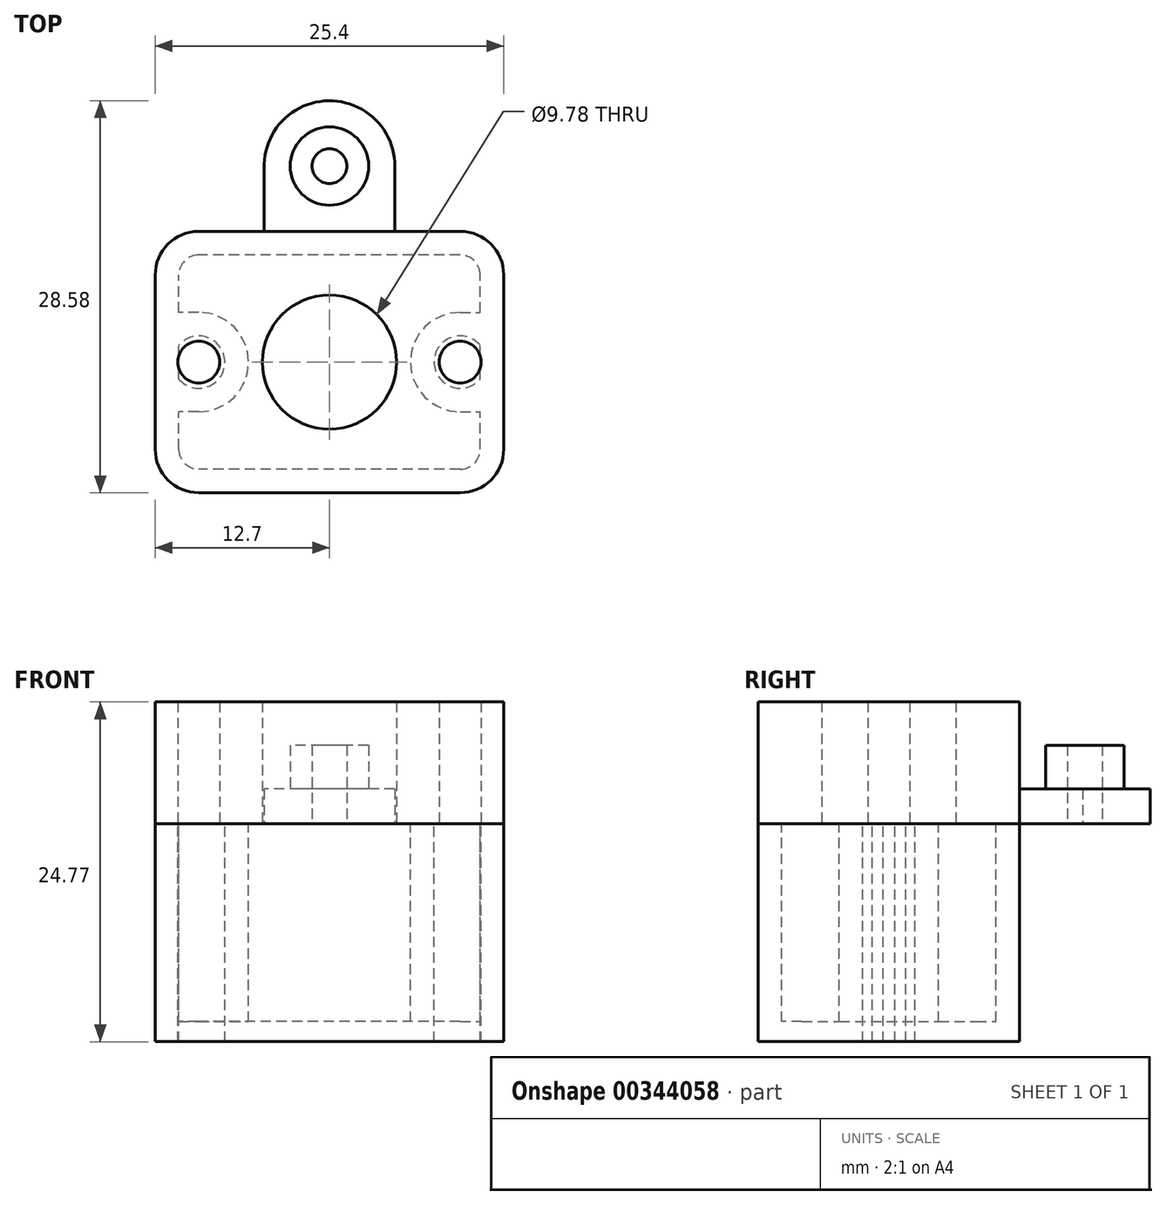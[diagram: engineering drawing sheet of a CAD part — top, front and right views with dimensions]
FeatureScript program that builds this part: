
annotation { "Feature Type Name" : "Feature", "Feature Type Description" : "" }
export const myFeature = defineFeature(function(context is Context, id is Id, definition is map)
    precondition{}
    {
        {
            var Q0;
            Q0=qCreatedBy(makeId("Top.planeOp"),FACE);
            var sketch = newSketch(context, id + "F0", { "sketchPlane" : qUnion([Q0])});
            skCircle(sketch, "E0", {"center": v(0, 0) * mm, "radius": 4.89 * mm});
            skLineSegment(sketch, "E1.bottom", {"start": v(9.52, -9.52) * mm, "end": v(-9.53, -9.53) * mm});
            skLineSegment(sketch, "E1.top", {"start": v(9.53, 9.53) * mm, "end": v(-9.53, 9.52) * mm});
            skLineSegment(sketch, "E1.left", {"start": v(12.7, -6.35) * mm, "end": v(12.7, 6.35) * mm});
            skLineSegment(sketch, "E1.right", {"start": v(-12.7, -6.35) * mm, "end": v(-12.7, 6.35) * mm});
            skPoint(sketch, "E2.visualSharp", {"position": v(-12.7, -9.53) * mm});
            skArc(sketch, "E2.filletArc", {"start": v(-12.7, -6.35) * mm, "mid": v(-11.77, -8.6) * mm, "end": v(-9.53, -9.53) * mm});
            skPoint(sketch, "E3.visualSharp", {"position": v(-12.7, 9.52) * mm});
            skArc(sketch, "E3.filletArc", {"start": v(-9.53, 9.52) * mm, "mid": v(-11.77, 8.6) * mm, "end": v(-12.7, 6.35) * mm});
            skPoint(sketch, "E4.visualSharp", {"position": v(12.7, -9.52) * mm});
            skArc(sketch, "E4.filletArc", {"start": v(9.52, -9.52) * mm, "mid": v(11.77, -8.6) * mm, "end": v(12.7, -6.35) * mm});
            skPoint(sketch, "E5.visualSharp", {"position": v(12.7, 9.53) * mm});
            skArc(sketch, "E5.filletArc", {"start": v(12.7, 6.35) * mm, "mid": v(11.77, 8.6) * mm, "end": v(9.53, 9.53) * mm});
            skCircle(sketch, "E6", {"center": v(-9.53, 0) * mm, "radius": 1.52 * mm});
            skPoint(sketch, "E6.centerSnap0", {"position": v(-12.7, 0) * mm});
            skCircle(sketch, "E7.MirrorC", {"center": v(9.53, 0) * mm, "radius": 1.52 * mm});
            skCircle(sketch, "E8", {"center": v(0, 14.29) * mm, "radius": 4.76 * mm});
            skLineSegment(sketch, "E9", {"start": v(-4.76, 14.12) * mm, "end": v(-4.76, 9.53) * mm});
            skLineSegment(sketch, "E10.bottom", {"start": v(4.76, 9.53) * mm, "end": v(-4.76, 9.53) * mm});
            skLineSegment(sketch, "E11", {"start": v(4.76, 9.53) * mm, "end": v(4.76, 14.26) * mm});
            skCircle(sketch, "E12", {"center": v(0, 14.29) * mm, "radius": 2.86 * mm});
            skCircle(sketch, "E13", {"center": v(0, 14.29) * mm, "radius": 1.27 * mm});
            skSolve(sketch);
        }
        {
            var Q0;
            Q0=makeQuery(id+"F0.imprint","IMPRINT",FACE,{"disambiguationData":[TD([[makeQuery(id+"F0.imprint","IMPRINT",EDGE,{"derivedFrom":sQuery(id+"F0.wireOp",EDGE,"E0")}),-1.0]])]});
            extrude(context, id + "F1", {"entities" : qUnion([Q0]), "depth" : 8.9 * mm});
        }
        {
            var Q0;
            {var subQ0=sQuery(id+"F0.wireOp",EDGE,"E11");Q0=makeQuery(id+"F0.imprint","IMPRINT",FACE,{"disambiguationData":[TD([[makeQuery(id+"F0.imprint","IMPRINT",EDGE,{"derivedFrom":subQ0}),1.0]])]});}
            var Q1;
            {var subQ0=sQuery(id+"F0.wireOp",EDGE,"E9");Q1=makeQuery(id+"F0.imprint","IMPRINT",FACE,{"disambiguationData":[TD([[makeQuery(id+"F0.imprint","IMPRINT",EDGE,{"derivedFrom":subQ0}),1.0]])]});}
            var Q2;
            Q2=makeQuery(id+"F0.imprint","IMPRINT",FACE,{"disambiguationData":[TD([[makeQuery(id+"F0.imprint","IMPRINT",EDGE,{"derivedFrom":sQuery(id+"F0.wireOp",EDGE,"E12")}),-1.0]])]});
            extrude(context, id + "F2", {"entities" : qUnion([Q0, Q1, Q2]), "operationType" : NewBodyOperationType.ADD, "depth" : 2.54 * mm});
        }
        {
            var Q0;
            Q0=makeQuery(id+"F0.imprint","IMPRINT",FACE,{"disambiguationData":[TD([[makeQuery(id+"F0.imprint","IMPRINT",EDGE,{"derivedFrom":sQuery(id+"F0.wireOp",EDGE,"E12")}),1.0]])]});
            extrude(context, id + "F3", {"entities" : qUnion([Q0]), "operationType" : NewBodyOperationType.ADD, "depth" : 5.7 * mm});
        }
        {
            var Q0;
            Q0=makeQuery(id+"F0.imprint","IMPRINT",FACE,{"disambiguationData":[TD([[makeQuery(id+"F0.imprint","IMPRINT",EDGE,{"derivedFrom":sQuery(id+"F0.wireOp",EDGE,"E0")}),-1.0]])]});
            var sketch = newSketch(context, id + "F4", { "sketchPlane" : qUnion([Q0])});
            skLineSegment(sketch, "E14.0", {"start": v(9.52, -9.52) * mm, "end": v(-9.53, -9.53) * mm});
            skArc(sketch, "E15.0", {"start": v(9.52, -9.52) * mm, "mid": v(11.77, -8.6) * mm, "end": v(12.7, -6.35) * mm});
            skLineSegment(sketch, "E16.0", {"start": v(12.7, -6.35) * mm, "end": v(12.7, 6.35) * mm});
            skArc(sketch, "E17.0", {"start": v(12.7, 6.35) * mm, "mid": v(11.77, 8.6) * mm, "end": v(9.53, 9.53) * mm});
            skLineSegment(sketch, "E18.0", {"start": v(9.53, 9.53) * mm, "end": v(-9.53, 9.52) * mm});
            skArc(sketch, "E19.0", {"start": v(-9.53, 9.52) * mm, "mid": v(-11.77, 8.6) * mm, "end": v(-12.7, 6.35) * mm});
            skLineSegment(sketch, "E20.0", {"start": v(-12.7, -6.35) * mm, "end": v(-12.7, 6.35) * mm});
            skArc(sketch, "E21.0", {"start": v(-12.7, -6.35) * mm, "mid": v(-11.77, -8.6) * mm, "end": v(-9.53, -9.53) * mm});
            skArc(sketch, "E22", {"start": v(10.99, 1.22) * mm, "mid": v(7.62, 0) * mm, "end": v(10.99, -1.22) * mm});
            skArc(sketch, "E23", {"start": v(-10.99, -1.22) * mm, "mid": v(-7.62, 0) * mm, "end": v(-10.99, 1.22) * mm});
            skArc(sketch, "E24.0", {"start": v(-10.99, -6.35) * mm, "mid": v(-10.56, -7.38) * mm, "end": v(-9.53, -7.81) * mm});
            skLineSegment(sketch, "E24.1", {"start": v(9.52, -7.81) * mm, "end": v(-9.53, -7.81) * mm});
            skLineSegment(sketch, "E24.2", {"start": v(-10.99, -6.35) * mm, "end": v(-10.99, 6.35) * mm});
            skArc(sketch, "E24.3", {"start": v(9.52, -7.81) * mm, "mid": v(10.56, -7.38) * mm, "end": v(10.99, -6.35) * mm});
            skArc(sketch, "E24.4", {"start": v(-9.53, 7.81) * mm, "mid": v(-10.56, 7.38) * mm, "end": v(-10.99, 6.35) * mm});
            skLineSegment(sketch, "E24.5", {"start": v(9.53, 7.81) * mm, "end": v(-9.53, 7.81) * mm});
            skArc(sketch, "E24.6", {"start": v(10.99, 6.35) * mm, "mid": v(10.56, 7.38) * mm, "end": v(9.53, 7.81) * mm});
            skLineSegment(sketch, "E24.7", {"start": v(10.99, -6.35) * mm, "end": v(10.99, 6.35) * mm});
            skArc(sketch, "E25.0", {"start": v(-9.53, -3.62) * mm, "mid": v(-5.9, 0) * mm, "end": v(-9.53, 3.62) * mm});
            skLineSegment(sketch, "E26", {"start": v(-9.53, 3.62) * mm, "end": v(-10.99, 3.62) * mm});
            skLineSegment(sketch, "E27", {"start": v(-9.53, -3.62) * mm, "end": v(-10.99, -3.62) * mm});
            skLineSegment(sketch, "E28.MirrorCS", {"start": v(9.53, -3.62) * mm, "end": v(10.99, -3.62) * mm});
            skArc(sketch, "E29.MirrorCS", {"start": v(9.53, -3.62) * mm, "mid": v(5.9, 0) * mm, "end": v(9.53, 3.62) * mm});
            skLineSegment(sketch, "E30.MirrorCS", {"start": v(9.53, 3.62) * mm, "end": v(10.99, 3.62) * mm});
            skSolve(sketch);
        }
        {
            var Q0;
            Q0=makeQuery(id+"F4.imprint","IMPRINT",FACE,{"disambiguationData":[TD([[makeQuery(id+"F4.imprint","IMPRINT",EDGE,{"derivedFrom":sQuery(id+"F4.wireOp",EDGE,"E14.0")}),-1.0]])]});
            var Q1;
            {var subQ1=sQuery(id+"F4.wireOp",EDGE,"E23");Q1=makeQuery(id+"F4.imprint","IMPRINT",FACE,{"disambiguationData":[TD([[makeQuery(id+"F4.imprint","IMPRINT",EDGE,{"derivedFrom":subQ1}),-1.0]])]});}
            var Q2;
            {var subQ1=sQuery(id+"F4.wireOp",EDGE,"E22");Q2=makeQuery(id+"F4.imprint","IMPRINT",FACE,{"disambiguationData":[TD([[makeQuery(id+"F4.imprint","IMPRINT",EDGE,{"derivedFrom":subQ1}),-1.0]])]});}
            var Q3;
            {var subQ2=sQuery(id+"F4.wireOp",EDGE,"E24.0");Q3=makeQuery(id+"F4.imprint","IMPRINT",FACE,{"disambiguationData":[TD([[makeQuery(id+"F4.imprint","IMPRINT",EDGE,{"derivedFrom":subQ2}),1.0]])]});}
            var Q4;
            Q4=makeQuery(id+"F4.imprint","IMPRINT",FACE,{"disambiguationData":[TD([[makeQuery(id+"F4.imprint","IMPRINT",EDGE,{"derivedFrom":makeQuery(id+"F0.imprint","IMPRINT",EDGE,{"derivedFrom":sQuery(id+"F0.wireOp",EDGE,"E0")})}),1.0]])]});
            extrude(context, id + "F5", {"entities" : qUnion([Q0, Q1, Q2, Q3, Q4]), "oppositeDirection" : true, "depth" : 15.88 * mm});
        }
        {
            var Q0;
            {var subQ2=sQuery(id+"F4.wireOp",EDGE,"E24.0");Q0=makeQuery(id+"F4.imprint","IMPRINT",FACE,{"disambiguationData":[TD([[makeQuery(id+"F4.imprint","IMPRINT",EDGE,{"derivedFrom":subQ2}),1.0]])]});}
            var Q1;
            Q1=makeQuery(id+"F4.imprint","IMPRINT",FACE,{"disambiguationData":[TD([[makeQuery(id+"F4.imprint","IMPRINT",EDGE,{"derivedFrom":makeQuery(id+"F0.imprint","IMPRINT",EDGE,{"derivedFrom":sQuery(id+"F0.wireOp",EDGE,"E0")})}),1.0]])]});
            extrude(context, id + "F6", {"entities" : qUnion([Q0, Q1]), "operationType" : NewBodyOperationType.REMOVE, "oppositeDirection" : true, "depth" : 14.4 * mm});
        }
    });
